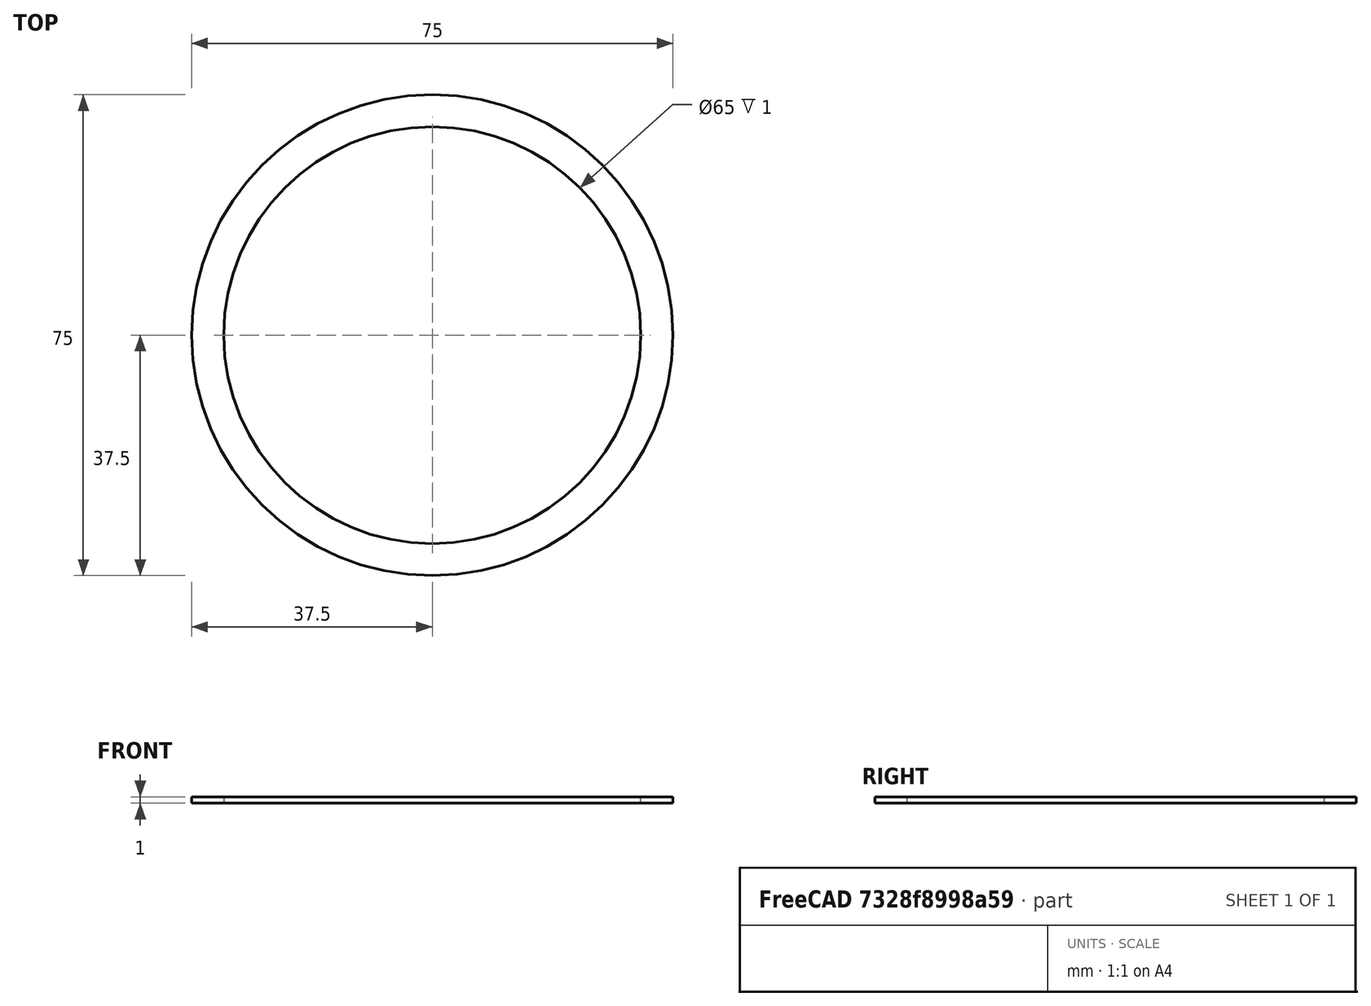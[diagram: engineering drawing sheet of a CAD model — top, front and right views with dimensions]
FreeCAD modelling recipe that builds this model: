
FCSTD DOCUMENT  (FreeCAD 0.19R24276 (Git))
Label: GT2_part_8_Ring_d65_d75_h1_for_turning
License: All rights reserved
LicenseURL: http://en.wikipedia.org/wiki/All_rights_reserved
objects: Sketcher::SketchObject×1, PartDesign::Pad×1, PartDesign::Body×1
note: 4 computed .brp shape members not serialized (recipe doc carries the construction recipe); baked Part::Feature solids carry a one-line shape summary decoded from their .brp

FEATURE [Sketcher::SketchObject] Sketch  label="Sketch_d65_d75"
  FullyConstrained = true
  MapMode = 5
  Support = -> [XY_Plane]
  sketch-geometry (2):
    g0: Circle CenterX=0 CenterY=0 CenterZ=0 NormalX=0 NormalY=0 NormalZ=1 AngleXU=0 Radius=32.5
    g1: Circle CenterX=0 CenterY=0 CenterZ=0 NormalX=0 NormalY=0 NormalZ=1 AngleXU=0 Radius=37.5
  constraints (4):
    c: Coincident(g0,g-1)
    c: Coincident(g1,g0)
    c: Diameter(g0) = 65
    c: Diameter(g1) = 75
FEATURE [PartDesign::Pad] Pad  label="Pad_h1"
  Direction = (1,1,1)
  Length = 1
  Length2 = 100
  Profile = -> Sketch
  Type = 0
FEATURE [PartDesign::Body] Body
  Group = -> [Sketch,Pad]
  Origin = -> Origin
  Tip = -> Pad
